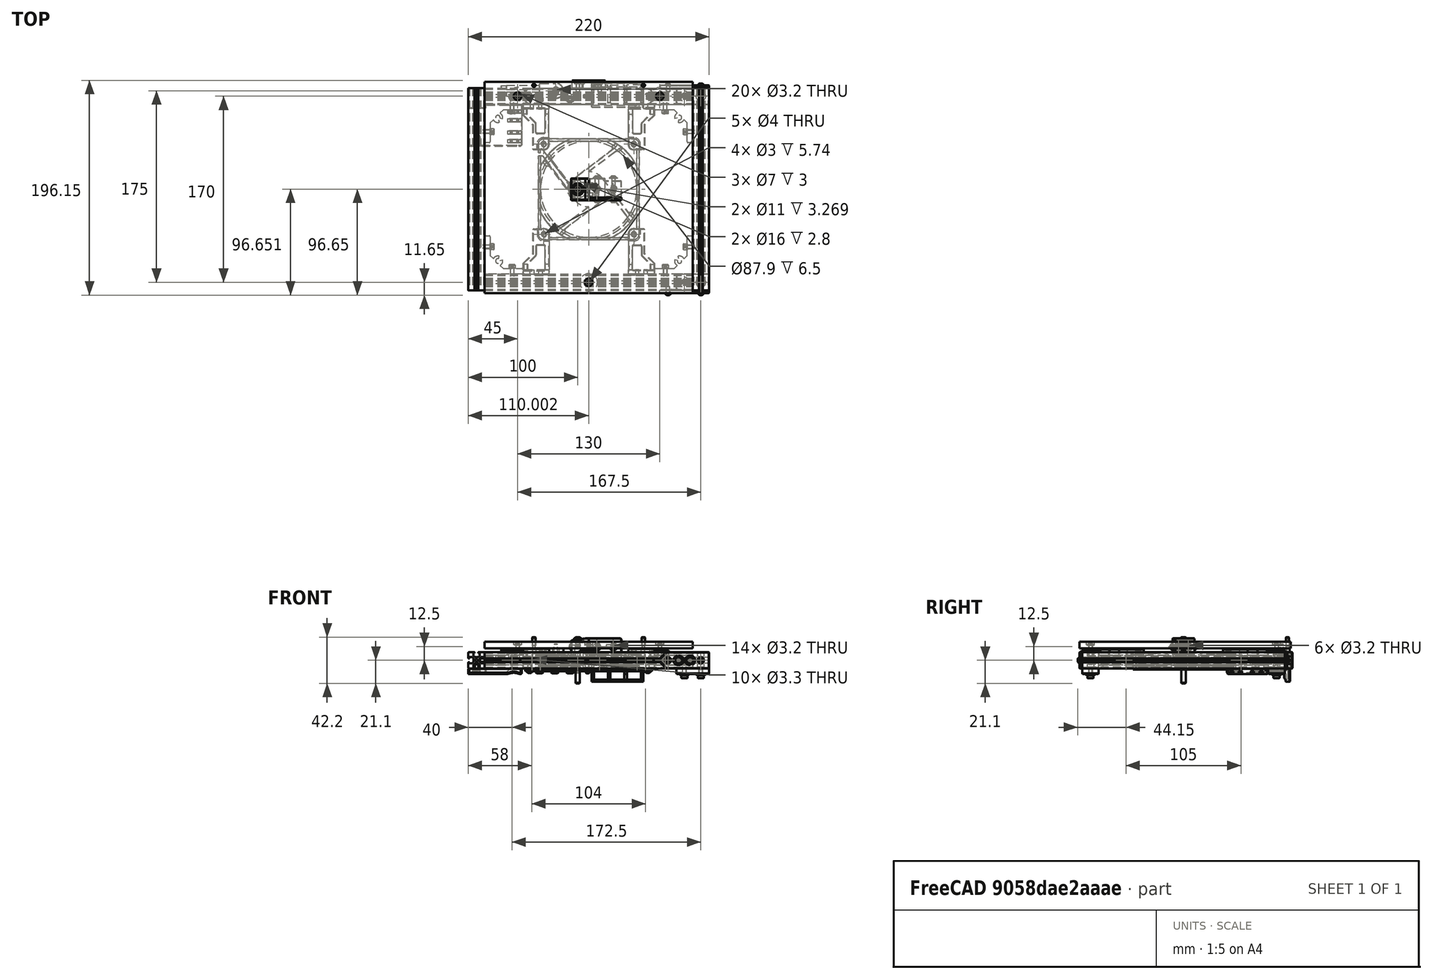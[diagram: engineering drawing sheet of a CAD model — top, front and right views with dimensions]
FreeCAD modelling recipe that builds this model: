
FCSTD DOCUMENT  (FreeCAD 0.19R24291 (Git))
Label: bed-assembly
License: Other
LicenseURL: GPL3
objects: Part::FeaturePython×88, Part::Feature×34, App::Part×8, PartDesign::CoordinateSystem×1
note: 123 computed .brp shape members not serialized (recipe doc carries the construction recipe); baked Part::Feature solids carry a one-line shape summary decoded from their .brp

FEATURE [Part::Feature] Cut028006004005011004003001010002002002001001  label="frame-end-cap"
  Placement = pos=(110,-95,-7.5) rot=(0,0.707107,0.707107;3.14159rad)
  shape: bbox 45 x 3.5 x 15 mm, 345 faces (baked)
FEATURE [Part::Feature] Chamfer004013007011015006009007001005003046001001  label="extrusion-connector"
  Placement = pos=(110,-77.5,-12.5) rot=(0,0,1;3.14159rad)
  shape: bbox 30 x 15 x 6 mm, 55 faces (baked)
FEATURE [Part::Feature] Extrude001001  label="1515-185mm001"
  Placement = pos=(102.5,92.5,-2.1e-14) rot=(1,0,0;1.5708rad)
  shape: bbox 15 x 185 x 15 mm, 71 faces (baked)
FEATURE [Part::Feature] Extrude001002  label="1515-190mm001"
  Placement = pos=(-95,-85,-2.11e-14) rot=(0,1,0;1.5708rad)
  shape: bbox 190 x 15 x 15 mm, 71 faces (baked)
FEATURE [Part::Feature] Extrude001005  label="1515-185mm003"
  Placement = pos=(-102.5,92.5,-2.1e-14) rot=(1,0,0;1.5708rad)
  shape: bbox 15 x 185 x 15 mm, 71 faces (baked)
FEATURE [Part::Feature] Extrude001006  label="1515-190mm003"
  Placement = pos=(-95,85,-2.11e-14) rot=(0,1,0;1.5708rad)
  shape: bbox 190 x 15 x 15 mm, 71 faces (baked)
FEATURE [Part::Feature] Part__Feature006  label="HBLTBS008"
  Placement = pos=(95,77.5,2.1e-14) rot=(0.707107,0,-0.707107;3.14159rad)
  shape: bbox 35 x 35 x 9 mm, 26 faces (baked)
FEATURE [Part::Feature] Part__Feature005  label="HBLTBS007"
  Placement = pos=(-95,77.5,-2.1e-14) rot=(0.57735,0.57735,-0.57735;2.0944rad)
  shape: bbox 35 x 35 x 9 mm, 26 faces (baked)
FEATURE [Part::Feature] Part__Feature008  label="HBLTBS010"
  Placement = pos=(-95,-77.5,-2.11e-14) rot=(0,1,0;1.5708rad)
  shape: bbox 35 x 35 x 9 mm, 26 faces (baked)
FEATURE [Part::Feature] Part__Feature007  label="HBLTBS009"
  Placement = pos=(95,-77.5,2.1e-14) rot=(0.57735,-0.57735,-0.57735;4.18879rad)
  shape: bbox 35 x 35 x 9 mm, 26 faces (baked)
FEATURE [Part::FeaturePython] Washer012  label="M3-Washer018"  # Fasteners workbench fastener (typed FeaturePython)
  Placement = pos=(-90,52.5,-2.1e-14) rot=(0,1,0;1.5708rad)
  baseObject = -> Part__Feature005 [Edge27]
  diameter = 4
  invert = false
  leftHanded = false
  matchOuter = true
  offset = 0
  type = 5
FEATURE [Part::FeaturePython] Washer013  label="M3-Washer019"  # Fasteners workbench fastener (typed FeaturePython)
  Placement = pos=(-70,72.5,-2.1e-14) rot=(1,0,0;1.5708rad)
  baseObject = -> Part__Feature005 [Edge62]
  diameter = 4
  invert = true
  leftHanded = false
  matchOuter = true
  offset = 0
  type = 5
FEATURE [Part::FeaturePython] Washer014  label="M3-Washer022"  # Fasteners workbench fastener (typed FeaturePython)
  Placement = pos=(90,52.5,2e-14) rot=(0,-1,0;1.5708rad)
  baseObject = -> Part__Feature006 [Edge62]
  diameter = 4
  invert = true
  leftHanded = false
  matchOuter = true
  offset = 0
  type = 5
FEATURE [Part::FeaturePython] Washer015  label="M3-Washer021"  # Fasteners workbench fastener (typed FeaturePython)
  Placement = pos=(70,72.5,1.5e-14) rot=(1,0,0;1.5708rad)
  baseObject = -> Part__Feature006 [Edge27]
  diameter = 4
  invert = false
  leftHanded = false
  matchOuter = true
  offset = 0
  type = 5
FEATURE [Part::FeaturePython] Washer016  label="M3-Washer023"  # Fasteners workbench fastener (typed FeaturePython)
  Placement = pos=(90,-52.5,2.1e-14) rot=(0,-1,0;1.5708rad)
  baseObject = -> Part__Feature007 [Edge27]
  diameter = 4
  invert = false
  leftHanded = false
  matchOuter = true
  offset = 0
  type = 5
FEATURE [Part::FeaturePython] Washer017  label="M3-Washer024"  # Fasteners workbench fastener (typed FeaturePython)
  Placement = pos=(70,-72.5,2.1e-14) rot=(-1,0,0;1.5708rad)
  baseObject = -> Part__Feature007 [Edge62]
  diameter = 4
  invert = true
  leftHanded = false
  matchOuter = true
  offset = 0
  type = 5
FEATURE [Part::FeaturePython] Washer018  label="M3-Washer025"  # Fasteners workbench fastener (typed FeaturePython)
  Placement = pos=(-70,-72.5,-2.1e-14) rot=(-1,0,0;1.5708rad)
  baseObject = -> Part__Feature008 [Edge27]
  diameter = 4
  invert = false
  leftHanded = false
  matchOuter = true
  offset = 0
  type = 5
FEATURE [Part::FeaturePython] Washer019  label="M3-Washer026"  # Fasteners workbench fastener (typed FeaturePython)
  Placement = pos=(-90,-52.5,-2.1e-14) rot=(0,1,0;1.5708rad)
  baseObject = -> Part__Feature008 [Edge62]
  diameter = 4
  invert = true
  leftHanded = false
  matchOuter = true
  offset = 0
  type = 5
FEATURE [Part::FeaturePython] Screw025  label="M3x10-Screw008"  # Fasteners workbench fastener (typed FeaturePython)
  Placement = pos=(-70,-71.95,-2.09e-14) rot=(-1,0,0;1.5708rad)
  baseObject = -> Washer018 [Edge1]
  diameter = 4
  invert = false
  leftHanded = false
  length = 3
  lengthCustom = 10
  matchOuter = true
  offset = 0
  thread = false
  type = 34
FEATURE [Part::FeaturePython] Screw026  label="M3x10-Screw009"  # Fasteners workbench fastener (typed FeaturePython)
  Placement = pos=(-89.45,-52.5,-2.09e-14) rot=(0,1,0;1.5708rad)
  baseObject = -> Washer019 [Edge1]
  diameter = 4
  invert = false
  leftHanded = false
  length = 3
  lengthCustom = 10
  matchOuter = true
  offset = 0
  thread = false
  type = 34
FEATURE [Part::FeaturePython] Screw027  label="M3x10-Screw010"  # Fasteners workbench fastener (typed FeaturePython)
  Placement = pos=(-89.45,52.5,-2.09e-14) rot=(0,1,0;1.5708rad)
  baseObject = -> Washer012 [Edge1]
  diameter = 4
  invert = false
  leftHanded = false
  length = 3
  lengthCustom = 10
  matchOuter = true
  offset = 0
  thread = false
  type = 34
FEATURE [Part::FeaturePython] Screw028  label="M3x10-Screw011"  # Fasteners workbench fastener (typed FeaturePython)
  Placement = pos=(-70,71.95,-2.09e-14) rot=(1,0,0;1.5708rad)
  baseObject = -> Washer013 [Edge1]
  diameter = 4
  invert = false
  leftHanded = false
  length = 3
  lengthCustom = 10
  matchOuter = true
  offset = 0
  thread = false
  type = 34
FEATURE [Part::FeaturePython] Screw029  label="M3x10-Screw012"  # Fasteners workbench fastener (typed FeaturePython)
  Placement = pos=(70,71.95,1.6e-14) rot=(1,0,0;1.5708rad)
  baseObject = -> Washer015 [Edge1]
  diameter = 4
  invert = false
  leftHanded = false
  length = 3
  lengthCustom = 10
  matchOuter = true
  offset = 0
  thread = false
  type = 34
FEATURE [Part::FeaturePython] Screw030  label="M3x10-Screw013"  # Fasteners workbench fastener (typed FeaturePython)
  Placement = pos=(89.45,52.5,2e-14) rot=(0,-1,0;1.5708rad)
  baseObject = -> Washer014 [Edge1]
  diameter = 4
  invert = false
  leftHanded = false
  length = 3
  lengthCustom = 10
  matchOuter = true
  offset = 0
  thread = false
  type = 34
FEATURE [Part::FeaturePython] Screw031  label="M3x10-Screw014"  # Fasteners workbench fastener (typed FeaturePython)
  Placement = pos=(89.45,-52.5,2.11e-14) rot=(0,-1,0;1.5708rad)
  baseObject = -> Washer016 [Edge1]
  diameter = 4
  invert = false
  leftHanded = false
  length = 3
  lengthCustom = 10
  matchOuter = true
  offset = 0
  thread = false
  type = 34
FEATURE [Part::FeaturePython] Screw032  label="M3x10-Screw015"  # Fasteners workbench fastener (typed FeaturePython)
  Placement = pos=(70,-71.95,2.11e-14) rot=(-1,0,0;1.5708rad)
  baseObject = -> Washer017 [Edge1]
  diameter = 4
  invert = false
  leftHanded = false
  length = 3
  lengthCustom = 10
  matchOuter = true
  offset = 0
  thread = false
  type = 34
FEATURE [Part::Feature] Chamfer004013007011015006009007001005003063003001002001002001005001006  label="extrusion-connector001"
  Placement = pos=(110,92.5,-12.5) rot=(0,0,1;3.14159rad)
  shape: bbox 30 x 15 x 6 mm, 55 faces (baked)
FEATURE [Part::FeaturePython] Washer020  label="M3-Washer027"  # Fasteners workbench fastener (typed FeaturePython)
  Placement = pos=(87.5,-85,-12.5) rot=(1,0,0;3.14159rad)
  baseObject = -> Chamfer004013007011015006009007001005003046001001 [Edge61]
  diameter = 1
  invert = true
  leftHanded = false
  matchOuter = true
  offset = 0
  type = 6
FEATURE [Part::FeaturePython] Washer021  label="M3-Washer028"  # Fasteners workbench fastener (typed FeaturePython)
  Placement = pos=(102.5,-85,-12.5) rot=(1,0,0;3.14159rad)
  baseObject = -> Chamfer004013007011015006009007001005003046001001 [Edge62]
  diameter = 1
  invert = true
  leftHanded = false
  matchOuter = true
  offset = 0
  type = 6
FEATURE [Part::FeaturePython] Washer022  label="M3-Washer029"  # Fasteners workbench fastener (typed FeaturePython)
  Placement = pos=(87.5,85,-12.5) rot=(1,0,0;3.14159rad)
  baseObject = -> Chamfer004013007011015006009007001005003063003001002001002001005001006 [Edge61]
  diameter = 1
  invert = true
  leftHanded = false
  matchOuter = true
  offset = 0
  type = 6
FEATURE [Part::FeaturePython] Washer023  label="M3-Washer030"  # Fasteners workbench fastener (typed FeaturePython)
  Placement = pos=(102.5,85,-12.5) rot=(1,0,0;3.14159rad)
  baseObject = -> Chamfer004013007011015006009007001005003063003001002001002001005001006 [Edge62]
  diameter = 1
  invert = true
  leftHanded = false
  matchOuter = true
  offset = 0
  type = 6
FEATURE [Part::FeaturePython] Screw033  label="M3x10-Screw016"  # Fasteners workbench fastener (typed FeaturePython)
  Placement = pos=(87.5,-85,-13.4) rot=(1,0,0;3.14159rad)
  baseObject = -> Washer020 [Edge1]
  diameter = 4
  invert = false
  leftHanded = false
  length = 3
  lengthCustom = 10
  matchOuter = true
  offset = 0
  thread = false
  type = 34
FEATURE [Part::FeaturePython] Screw034  label="M3x10-Screw017"  # Fasteners workbench fastener (typed FeaturePython)
  Placement = pos=(102.5,-85,-13.4) rot=(1,0,0;3.14159rad)
  baseObject = -> Washer021 [Edge1]
  diameter = 4
  invert = false
  leftHanded = false
  length = 3
  lengthCustom = 10
  matchOuter = true
  offset = 0
  thread = false
  type = 34
FEATURE [Part::FeaturePython] Screw035  label="M3x10-Screw018"  # Fasteners workbench fastener (typed FeaturePython)
  Placement = pos=(87.5,85,-13.4) rot=(1,0,0;3.14159rad)
  baseObject = -> Washer022 [Edge1]
  diameter = 4
  invert = false
  leftHanded = false
  length = 3
  lengthCustom = 10
  matchOuter = true
  offset = 0
  thread = false
  type = 34
FEATURE [Part::FeaturePython] Screw036  label="M3x10-Screw019"  # Fasteners workbench fastener (typed FeaturePython)
  Placement = pos=(102.5,85,-13.4) rot=(1,0,0;3.14159rad)
  baseObject = -> Washer023 [Edge1]
  diameter = 4
  invert = false
  leftHanded = false
  length = 3
  lengthCustom = 10
  matchOuter = true
  offset = 0
  thread = false
  type = 34
FEATURE [Part::Feature] Cut028006004005011004003001010002002002001007  label="frame-end-cap001"
  Placement = pos=(110,95,7.5) rot=(0,0.707107,-0.707107;3.14159rad)
  shape: bbox 45 x 3.5 x 15 mm, 345 faces (baked)
FEATURE [Part::FeaturePython] Screw037  label="M3x6-Screw006"  # Fasteners workbench fastener (typed FeaturePython)
  Placement = pos=(102.5,95,-1.07e-13) rot=(-1,0,0;1.5708rad)
  baseObject = -> Cut028006004005011004003001010002002002001007 [Edge235]
  diameter = 1
  invert = true
  leftHanded = false
  length = 0
  lengthCustom = 6
  matchOuter = true
  offset = 0
  thread = false
  type = 40
FEATURE [Part::FeaturePython] Screw038  label="M3x6-Screw007"  # Fasteners workbench fastener (typed FeaturePython)
  Placement = pos=(72.5,95,-1.04e-13) rot=(-1,0,0;1.5708rad)
  baseObject = -> Cut028006004005011004003001010002002002001007 [Edge236]
  diameter = 1
  invert = true
  leftHanded = false
  length = 0
  lengthCustom = 6
  matchOuter = true
  offset = 0
  thread = false
  type = 40
FEATURE [Part::FeaturePython] Screw039  label="M3x6-Screw008"  # Fasteners workbench fastener (typed FeaturePython)
  Placement = pos=(72.5,-95,-6.8e-14) rot=(1,0,0;1.5708rad)
  baseObject = -> Cut028006004005011004003001010002002002001001 [Edge236]
  diameter = 1
  invert = true
  leftHanded = false
  length = 0
  lengthCustom = 6
  matchOuter = true
  offset = 0
  thread = false
  type = 40
FEATURE [Part::FeaturePython] Screw040  label="M3x6-Screw009"  # Fasteners workbench fastener (typed FeaturePython)
  Placement = pos=(102.5,-95,-6.5e-14) rot=(1,0,0;1.5708rad)
  baseObject = -> Cut028006004005011004003001010002002002001001 [Edge235]
  diameter = 1
  invert = true
  leftHanded = false
  length = 0
  lengthCustom = 6
  matchOuter = true
  offset = 0
  thread = false
  type = 40
FEATURE [App::Part] Part003  label="bed-frame"
  Group = -> [Extrude001001,Extrude001002,Extrude001005,Extrude001006,Part__Feature006,Part__Feature005,Part__Feature008,Part__Feature007,Chamfer004013007011015006009007001005003046001001,Chamfer004013007011015006009007001005003063003001002001002001005001006,Washer012,Washer013,Washer014,Washer015,Washer016,Washer017,Washer018,Washer019,Screw025,Screw026,Screw027,Screw028,Screw029,Screw030,Screw031,Screw032,+14 more]
  Origin = -> Origin003
FEATURE [Part::Feature] Pocket002  label="aluminum-plate-190x193x6"
  Placement = pos=(0,0,11) rot=(0,0,1;0rad)
  shape: bbox 190 x 193 x 6 mm, 17 faces (baked)
FEATURE [Part::Feature] Cut002  label="silicon-spacer001"
  Placement = pos=(-65,85,0) rot=(0,0,1;0rad)
  shape: bbox 16 x 16 x 9 mm, 4 faces (baked)
FEATURE [Part::Feature] Cut003  label="silicon-spacer002"
  Placement = pos=(0,-85,0) rot=(0,0,1;0rad)
  shape: bbox 16 x 16 x 9 mm, 4 faces (baked)
FEATURE [Part::Feature] Cut001  label="silicon-spacer"
  Placement = pos=(65,85,0) rot=(0,0,1;0rad)
  shape: bbox 16 x 16 x 9 mm, 4 faces (baked)
FEATURE [Part::FeaturePython] Washer024  label="M3-Washer031"  # Fasteners workbench fastener (typed FeaturePython)
  Placement = pos=(-65,85,9) rot=(0,0,1;0rad)
  baseObject = -> Cut002 [Edge4]
  diameter = 1
  invert = false
  leftHanded = false
  matchOuter = true
  offset = 0
  type = 6
FEATURE [Part::FeaturePython] Washer025  label="M3-Washer032"  # Fasteners workbench fastener (typed FeaturePython)
  Placement = pos=(65,85,9) rot=(0,0,1;0rad)
  baseObject = -> Cut001 [Edge4]
  diameter = 1
  invert = false
  leftHanded = false
  matchOuter = true
  offset = 0
  type = 6
FEATURE [Part::FeaturePython] Washer026  label="M3-Washer033"  # Fasteners workbench fastener (typed FeaturePython)
  Placement = pos=(0,-85,9) rot=(0,0,1;0rad)
  baseObject = -> Cut003 [Edge4]
  diameter = 1
  invert = false
  leftHanded = false
  matchOuter = true
  offset = 0
  type = 6
FEATURE [Part::FeaturePython] Washer027  label="M3-Washer034"  # Fasteners workbench fastener (typed FeaturePython)
  Placement = pos=(-65,85,9.9) rot=(0,0,1;0rad)
  baseObject = -> Washer024 [Edge1]
  diameter = 1
  invert = false
  leftHanded = false
  matchOuter = true
  offset = 0
  type = 6
FEATURE [Part::FeaturePython] Washer028  label="M3-Washer035"  # Fasteners workbench fastener (typed FeaturePython)
  Placement = pos=(0,-85,9.9) rot=(0,0,1;0rad)
  baseObject = -> Washer026 [Edge1]
  diameter = 1
  invert = false
  leftHanded = false
  matchOuter = true
  offset = 0
  type = 6
FEATURE [Part::FeaturePython] Washer029  label="M3-Washer036"  # Fasteners workbench fastener (typed FeaturePython)
  Placement = pos=(65,85,9.9) rot=(0,0,1;0rad)
  baseObject = -> Washer025 [Edge1]
  diameter = 1
  invert = false
  leftHanded = false
  matchOuter = true
  offset = 0
  type = 6
FEATURE [Part::FeaturePython] Screw041  label="M3x16-Screw"  # Fasteners workbench fastener (typed FeaturePython)
  Placement = pos=(-65,85,13.8) rot=(0,0,1;0rad)
  baseObject = -> Washer027 [Edge1]
  diameter = 1
  invert = false
  leftHanded = false
  length = 5
  lengthCustom = 16
  matchOuter = true
  offset = 3
  thread = false
  type = 40
FEATURE [Part::FeaturePython] Screw042  label="M3x16-Screw003"  # Fasteners workbench fastener (typed FeaturePython)
  Placement = pos=(65,85,13.8) rot=(0,0,1;0rad)
  baseObject = -> Washer029 [Edge1]
  diameter = 1
  invert = false
  leftHanded = false
  length = 5
  lengthCustom = 16
  matchOuter = true
  offset = 3
  thread = false
  type = 40
FEATURE [Part::FeaturePython] Screw043  label="M3x16-Screw004"  # Fasteners workbench fastener (typed FeaturePython)
  Placement = pos=(0,-85,13.8) rot=(0,0,1;0rad)
  baseObject = -> Washer028 [Edge1]
  diameter = 1
  invert = false
  leftHanded = false
  length = 5
  lengthCustom = 16
  matchOuter = true
  offset = 3
  thread = false
  type = 40
FEATURE [Part::FeaturePython] Screw044  label="M3x8-Screw002"  # Fasteners workbench fastener (typed FeaturePython)
  Placement = pos=(-50,95,21) rot=(0,0,1;0rad)
  baseObject = -> Pocket002 [Edge21]
  diameter = 6
  invert = false
  leftHanded = false
  length = 5
  lengthCustom = 8
  matchOuter = true
  offset = 4
  thread = false
  type = 30
FEATURE [Part::FeaturePython] Screw045  label="M3x8-Screw003"  # Fasteners workbench fastener (typed FeaturePython)
  Placement = pos=(50,95,21) rot=(0,0,1;0rad)
  baseObject = -> Pocket002 [Edge20]
  diameter = 6
  invert = false
  leftHanded = false
  length = 5
  lengthCustom = 8
  matchOuter = true
  offset = 4
  thread = false
  type = 30
FEATURE [Part::Feature] Part__Feature004  label="thermal-fuse-180"
  Placement = pos=(-30,90,11.18) rot=(0,1,0;1.5708rad)
  shape: bbox 57 x 14 x 6 mm, 31 faces (baked)
FEATURE [Part::FeaturePython] Washer030  label="M3-Washer037"  # Fasteners workbench fastener (typed FeaturePython)
  Placement = pos=(-30,90,5.18) rot=(1,0,0;3.14159rad)
  baseObject = -> Part__Feature004 [Edge27]
  diameter = 4
  invert = false
  leftHanded = false
  matchOuter = true
  offset = 0
  type = 5
FEATURE [Part::FeaturePython] Screw046  label="M3x10-Screw020"  # Fasteners workbench fastener (typed FeaturePython)
  Placement = pos=(-30,90,4.63) rot=(1,0,0;3.14159rad)
  baseObject = -> Washer030 [Edge1]
  diameter = 4
  invert = false
  leftHanded = false
  length = 3
  lengthCustom = 10
  matchOuter = true
  offset = 0
  thread = false
  type = 34
FEATURE [App::Part] Part004  label="bed-plate"
  Group = -> [Pocket002,Cut002,Cut003,Cut001,Washer024,Washer025,Washer026,Washer027,Washer028,Washer029,Screw041,Screw042,Screw043,Screw044,Screw045,Part__Feature004,Washer030,Screw046]
  Origin = -> Origin004
  Placement = pos=(0,0,7.5) rot=(0,0,1;0rad)
FEATURE [Part::Feature] Part__Mirroring002  label="wago-mounter"
  Placement = pos=(0,75,-7.5) rot=(1,0,0;3.14159rad)
  shape: bbox 116 x 22.25 x 12.2 mm, 276 faces (baked)
FEATURE [Part::Feature] Body001001001  label="bed-cable-supporter"
  Placement = pos=(0,92.5,-7.5) rot=(0,0,1;0rad)
  shape: bbox 30 x 8 x 15 mm, 58 faces (baked)
FEATURE [Part::FeaturePython] Screw047  label="M3x6-Screw013"  # Fasteners workbench fastener (typed FeaturePython)
  Placement = pos=(-54,85,-10) rot=(1,0,0;3.14159rad)
  baseObject = -> Part__Mirroring002 [Edge150]
  diameter = 1
  invert = true
  leftHanded = false
  length = 0
  lengthCustom = 6
  matchOuter = true
  offset = 0
  thread = false
  type = 40
FEATURE [Part::FeaturePython] Screw048  label="M3x6-Screw014"  # Fasteners workbench fastener (typed FeaturePython)
  Placement = pos=(-10,85,-10) rot=(1,0,0;3.14159rad)
  baseObject = -> Part__Mirroring002 [Edge178]
  diameter = 1
  invert = true
  leftHanded = false
  length = 0
  lengthCustom = 6
  matchOuter = true
  offset = 0
  thread = false
  type = 40
FEATURE [Part::FeaturePython] Screw049  label="M3x6-Screw015"  # Fasteners workbench fastener (typed FeaturePython)
  Placement = pos=(54,85,-10) rot=(1,0,0;3.14159rad)
  baseObject = -> Part__Mirroring002 [Edge651]
  diameter = 1
  invert = true
  leftHanded = false
  length = 0
  lengthCustom = 6
  matchOuter = true
  offset = 0
  thread = false
  type = 40
FEATURE [Part::FeaturePython] Screw052  label="M3x8-Screw001"  # Fasteners workbench fastener (typed FeaturePython)
  Placement = pos=(-10,96.5,-1e-15) rot=(-1,0,0;1.5708rad)
  baseObject = -> Body001001001 [Edge118]
  diameter = 4
  invert = true
  leftHanded = false
  length = 2
  lengthCustom = 8
  matchOuter = true
  offset = 0
  thread = false
  type = 34
FEATURE [Part::FeaturePython] Screw053  label="M3x8-Screw"  # Fasteners workbench fastener (typed FeaturePython)
  Placement = pos=(10,96.5,-1e-15) rot=(-1,0,0;1.5708rad)
  baseObject = -> Body001001001 [Edge80]
  diameter = 4
  invert = true
  leftHanded = false
  length = 2
  lengthCustom = 8
  matchOuter = true
  offset = 0
  thread = false
  type = 34
FEATURE [Part::Feature] Body002001003  label="1515-92mm-fan-mount002"
  Placement = pos=(-59.75,-77.5,10.5) rot=(1,0,0;3.14159rad)
  shape: bbox 23.75 x 42.25 x 18 mm, 72 faces (baked)
FEATURE [Part::Feature] Part__Mirroring001003  label="1515-92mm-fan-mount001 (Mirror #1)002"
  Placement = pos=(-60,77.5,10.5) rot=(1,0,0;3.14159rad)
  shape: bbox 23.75 x 42.25 x 18 mm, 72 faces (baked)
FEATURE [Part::Feature] Body002001  label="1515-92mm-fan-mount001"
  Placement = pos=(60,77.5,10.5) rot=(0,1,0;3.14159rad)
  shape: bbox 23.75 x 42.25 x 18 mm, 72 faces (baked)
FEATURE [Part::Feature] Part__Mirroring003  label="1515-92mm-fan-mount001 (Mirror #1)001"
  Placement = pos=(60,-77.5,10.5) rot=(0,1,0;3.14159rad)
  shape: bbox 23.75 x 42.25 x 18 mm, 72 faces (baked)
FEATURE [Part::Feature] Fusion001001  label="92mm-slim-fan"
  Placement = pos=(0,2e-15,7.5) rot=(1,0,0;3.14159rad)
  shape: bbox 118.8 x 118.8 x 17.52 mm, 159 faces (baked)
FEATURE [Part::FeaturePython] HeatSet009  label="M3x4-HeatSet006"  # WARN: FeaturePython — macro-defined, semantics opaque (R4)
  Placement = pos=(41.25,-41.25,5.5) rot=(1,0,0;3.14159rad)
  baseObject = -> Part__Mirroring003 [Edge125]
  diameter = 2
  invert = true
  leftHanded = false
  offset = 0
FEATURE [Part::FeaturePython] HeatSet010  label="M3x4-HeatSet007"  # WARN: FeaturePython — macro-defined, semantics opaque (R4)
  Placement = pos=(-41,-41.25,5.5) rot=(1,0,0;3.14159rad)
  baseObject = -> Body002001003 [Edge125]
  diameter = 2
  invert = false
  leftHanded = false
  offset = 0
FEATURE [Part::FeaturePython] HeatSet011  label="M3x4-HeatSet008"  # WARN: FeaturePython — macro-defined, semantics opaque (R4)
  Placement = pos=(-41.25,41.25,5.5) rot=(1,0,0;3.14159rad)
  baseObject = -> Part__Mirroring001003 [Edge125]
  diameter = 2
  invert = true
  leftHanded = false
  offset = 0
FEATURE [Part::FeaturePython] HeatSet012  label="M3x4-HeatSet009"  # WARN: FeaturePython — macro-defined, semantics opaque (R4)
  Placement = pos=(41.25,41.25,5.5) rot=(1,0,0;3.14159rad)
  baseObject = -> Body002001 [Edge125]
  diameter = 2
  invert = false
  leftHanded = false
  offset = 0
FEATURE [App::Part] Part006  label="bed-fan"
  Group = -> [Body002001003,Part__Mirroring001003,Body002001,Part__Mirroring003,Fusion001001,HeatSet009,HeatSet010,HeatSet011,HeatSet012]
  Origin = -> Origin006
FEATURE [PartDesign::CoordinateSystem] LCS_0  label="LCS_bed"
  AttacherType = Attacher::AttachEngine3D
  MapMode = 2
  Support = -> [X_Axis007]
FEATURE [Part::FeaturePython] Screw054  label="M3x6-Screw018"  # Fasteners workbench fastener (typed FeaturePython)
  Placement = pos=(-102.5,67.5,-9.5) rot=(1,0,0;3.14159rad)
  diameter = 1
  invert = false
  leftHanded = false
  length = 0
  lengthCustom = 6
  matchOuter = true
  offset = 0
  thread = false
  type = 40
FEATURE [Part::FeaturePython] Screw055  label="M3x6-Screw019"  # Fasteners workbench fastener (typed FeaturePython)
  Placement = pos=(-102.5,46.5,-9.5) rot=(1,0,0;3.14159rad)
  diameter = 1
  invert = false
  leftHanded = false
  length = 0
  lengthCustom = 6
  matchOuter = true
  offset = 0
  thread = false
  type = 40
FEATURE [Part::Feature] Fusion001001001  label="bed-cable-mounter"
  Placement = pos=(-110,77.5,-12.5) rot=(1,0,0;1.5708rad)
  shape: bbox 49 x 38 x 5 mm, 109 faces (baked)
FEATURE [App::Part] Part005  label="bed-cable-management"
  Group = -> [Part__Mirroring002,Body001001001,Screw047,Screw048,Screw049,Screw053,Screw052,Screw054,Screw055,Fusion001001001]
  Origin = -> Origin005
FEATURE [Part::Feature] Chamfer004013007011015006009007001005003063003001002001002001007002017001  label="front-left-arm"
  shape: bbox 49.5 x 20 x 20 mm, 120 faces (baked)
FEATURE [Part::Feature] Part__Mirroring001001  label="back-left-arm"
  Placement = pos=(0,0,0) rot=(0,0,1;3.14159rad)
  shape: bbox 49.5 x 20 x 20 mm, 120 faces (baked)
FEATURE [Part::Feature] Body004001  label="middle-right-arm"
  shape: bbox 34.5 x 20 x 20 mm, 89 faces (baked)
FEATURE [Part::Feature] Tube001001  label="silicon-spacer-16ODx4UDx9H001"
  Placement = pos=(-10,0,-4) rot=(0,0,1;0rad)
  shape: bbox 16 x 16 x 7 mm, 4 faces (baked)
FEATURE [Part::Feature] Tube001002  label="silicon-spacer-16ODx4UDx9H002"
  Placement = pos=(-10,0,-4) rot=(0,0,1;0rad)
  shape: bbox 16 x 16 x 7 mm, 4 faces (baked)
FEATURE [Part::Feature] Tube001003  label="silicon-spacer-16ODx4UDx9H003"
  Placement = pos=(-10,0,-4) rot=(0,0,1;0rad)
  shape: bbox 16 x 16 x 7 mm, 4 faces (baked)
FEATURE [Part::Feature] Tube001002001  label="O-ring-10ODx4IDx2H001"
  Placement = pos=(-10,0,16) rot=(0,0,1;0rad)
  shape: bbox 10 x 10 x 2 mm, 4 faces (baked)
FEATURE [Part::Feature] Tube001002002  label="O-ring-10ODx4IDx2H002"
  Placement = pos=(-10,0,16) rot=(0,0,1;0rad)
  shape: bbox 10 x 10 x 2 mm, 4 faces (baked)
FEATURE [Part::Feature] Tube001002003  label="O-ring-10ODx4IDx2H003"
  Placement = pos=(-10,0,16) rot=(0,0,1;0rad)
  shape: bbox 10 x 10 x 2 mm, 4 faces (baked)
FEATURE [Part::FeaturePython] Washer  label="M3-Washer"  # Fasteners workbench fastener (typed FeaturePython)
  Placement = pos=(7.5,0,0) rot=(-1,0,0;3.14159rad)
  baseObject = -> Chamfer004013007011015006009007001005003063003001002001002001007002017001 [Edge223]
  diameter = 4
  invert = false
  leftHanded = false
  matchOuter = false
  offset = 0
  type = 3
FEATURE [Part::FeaturePython] Washer031  label="M3-Washer038"  # Fasteners workbench fastener (typed FeaturePython)
  Placement = pos=(22.5,0,0) rot=(-1,0,0;3.14159rad)
  baseObject = -> Chamfer004013007011015006009007001005003063003001002001002001007002017001 [Edge222]
  diameter = 4
  invert = false
  leftHanded = false
  matchOuter = false
  offset = 0
  type = 3
FEATURE [Part::FeaturePython] Washer032  label="M3-Washer042"  # Fasteners workbench fastener (typed FeaturePython)
  Placement = pos=(7.5,-9e-16,0) rot=(-1,0,0;3.14159rad)
  baseObject = -> Part__Mirroring001001 [Edge223]
  diameter = 4
  invert = true
  leftHanded = false
  matchOuter = false
  offset = 0
  type = 3
FEATURE [Part::FeaturePython] Washer033  label="M3-Washer043"  # Fasteners workbench fastener (typed FeaturePython)
  Placement = pos=(22.5,-2.8e-15,0) rot=(-1,0,0;3.14159rad)
  baseObject = -> Part__Mirroring001001 [Edge222]
  diameter = 4
  invert = true
  leftHanded = false
  matchOuter = false
  offset = 0
  type = 3
FEATURE [Part::FeaturePython] Washer034  label="M3-Washer041"  # Fasteners workbench fastener (typed FeaturePython)
  Placement = pos=(7.5,0,0) rot=(-1,0,0;3.14159rad)
  baseObject = -> Body004001 [Edge68]
  diameter = 4
  invert = false
  leftHanded = false
  matchOuter = false
  offset = 0
  type = 3
FEATURE [Part::FeaturePython] Screw  label="M3x10-Screw"  # Fasteners workbench fastener (typed FeaturePython)
  Placement = pos=(7.5,1e-16,-0.55) rot=(-1,0,0;3.14159rad)
  baseObject = -> Washer [Edge1]
  diameter = 3
  invert = false
  leftHanded = false
  length = 3
  lengthCustom = 10
  matchOuter = false
  offset = 0
  thread = false
  type = 22
FEATURE [Part::FeaturePython] Screw056  label="M3x10-Screw021"  # Fasteners workbench fastener (typed FeaturePython)
  Placement = pos=(22.5,1e-16,-0.55) rot=(-1,0,0;3.14159rad)
  baseObject = -> Washer031 [Edge1]
  diameter = 3
  invert = false
  leftHanded = false
  length = 3
  lengthCustom = 10
  matchOuter = false
  offset = 0
  thread = false
  type = 22
FEATURE [Part::FeaturePython] Screw057  label="M3x10-Screw022"  # Fasteners workbench fastener (typed FeaturePython)
  Placement = pos=(7.5,-9e-16,-0.55) rot=(-1,0,0;3.14159rad)
  baseObject = -> Washer032 [Edge1]
  diameter = 4
  invert = false
  leftHanded = false
  length = 3
  lengthCustom = 10
  matchOuter = false
  offset = 0
  thread = false
  type = 36
FEATURE [Part::FeaturePython] Screw058  label="M3x10-Screw023"  # Fasteners workbench fastener (typed FeaturePython)
  Placement = pos=(22.5,-2.7e-15,-0.55) rot=(-1,0,0;3.14159rad)
  baseObject = -> Washer033 [Edge1]
  diameter = 4
  invert = false
  leftHanded = false
  length = 3
  lengthCustom = 10
  matchOuter = false
  offset = 0
  thread = false
  type = 36
FEATURE [Part::FeaturePython] Screw059  label="M3x10-Screw024"  # Fasteners workbench fastener (typed FeaturePython)
  Placement = pos=(7.5,1e-16,-0.55) rot=(-1,0,0;3.14159rad)
  baseObject = -> Washer034 [Edge1]
  diameter = 4
  invert = false
  leftHanded = false
  length = 3
  lengthCustom = 10
  matchOuter = false
  offset = 0
  thread = false
  type = 36
FEATURE [Part::FeaturePython] Washer035  label="M3-Washer044"  # Fasteners workbench fastener (typed FeaturePython)
  Placement = pos=(7.5,-10,12.5) rot=(1,0,0;1.5708rad)
  baseObject = -> Chamfer004013007011015006009007001005003063003001002001002001007002017001 [Edge59]
  diameter = 4
  invert = false
  leftHanded = false
  matchOuter = true
  offset = 0
  type = 3
FEATURE [Part::FeaturePython] Washer036  label="M3-Washer045"  # Fasteners workbench fastener (typed FeaturePython)
  Placement = pos=(22.5,-10,12.5) rot=(1,0,0;1.5708rad)
  baseObject = -> Chamfer004013007011015006009007001005003063003001002001002001007002017001 [Edge60]
  diameter = 4
  invert = false
  leftHanded = false
  matchOuter = true
  offset = 0
  type = 3
FEATURE [Part::FeaturePython] Washer037  label="M3-Washer048"  # Fasteners workbench fastener (typed FeaturePython)
  Placement = pos=(22.5,10,12.5) rot=(-1,0,0;1.5708rad)
  baseObject = -> Part__Mirroring001001 [Edge60]
  diameter = 4
  invert = true
  leftHanded = false
  matchOuter = true
  offset = 0
  type = 3
FEATURE [Part::FeaturePython] Washer038  label="M3-Washer049"  # Fasteners workbench fastener (typed FeaturePython)
  Placement = pos=(7.5,10,12.5) rot=(-1,0,0;1.5708rad)
  baseObject = -> Part__Mirroring001001 [Edge59]
  diameter = 4
  invert = true
  leftHanded = false
  matchOuter = true
  offset = 0
  type = 3
FEATURE [Part::FeaturePython] Screw060  label="M3x8-Screw004"  # Fasteners workbench fastener (typed FeaturePython)
  Placement = pos=(7.5,-10.55,12.5) rot=(1,0,0;1.5708rad)
  baseObject = -> Washer035 [Edge1]
  diameter = 1
  invert = false
  leftHanded = false
  length = 1
  lengthCustom = 8
  matchOuter = true
  offset = 0
  thread = false
  type = 42
FEATURE [Part::FeaturePython] Screw061  label="M3x8-Screw005"  # Fasteners workbench fastener (typed FeaturePython)
  Placement = pos=(22.5,-10.55,12.5) rot=(1,0,0;1.5708rad)
  baseObject = -> Washer036 [Edge1]
  diameter = 1
  invert = false
  leftHanded = false
  length = 1
  lengthCustom = 8
  matchOuter = true
  offset = 0
  thread = false
  type = 42
FEATURE [Part::FeaturePython] Screw062  label="M3x8-Screw006"  # Fasteners workbench fastener (typed FeaturePython)
  Placement = pos=(22.5,10.55,12.5) rot=(-1,0,0;1.5708rad)
  baseObject = -> Washer037 [Edge1]
  diameter = 1
  invert = false
  leftHanded = false
  length = 1
  lengthCustom = 8
  matchOuter = true
  offset = 0
  thread = false
  type = 42
FEATURE [Part::FeaturePython] Screw063  label="M3x8-Screw007"  # Fasteners workbench fastener (typed FeaturePython)
  Placement = pos=(7.5,10.55,12.5) rot=(-1,0,0;1.5708rad)
  baseObject = -> Washer038 [Edge1]
  diameter = 1
  invert = false
  leftHanded = false
  length = 1
  lengthCustom = 8
  matchOuter = true
  offset = 0
  thread = false
  type = 42
FEATURE [Part::FeaturePython] Washer039  label="M4-OD10-Washer-001"  # Fasteners workbench fastener (typed FeaturePython)
  Placement = pos=(-10,0,18) rot=(0,0,1;0rad)
  baseObject = -> Tube001002001 [Edge4]
  diameter = 5
  invert = false
  leftHanded = false
  matchOuter = true
  offset = 0
  type = 3
FEATURE [Part::FeaturePython] Washer040  label="M4-OD10-Washer"  # Fasteners workbench fastener (typed FeaturePython)
  Placement = pos=(-10,0,18) rot=(0,0,1;0rad)
  baseObject = -> Tube001002002 [Edge4]
  diameter = 5
  invert = false
  leftHanded = false
  matchOuter = true
  offset = 0
  type = 3
FEATURE [Part::FeaturePython] Washer041  label="M4-OD10-Washer001"  # Fasteners workbench fastener (typed FeaturePython)
  Placement = pos=(-10,0,18) rot=(0,0,1;0rad)
  baseObject = -> Tube001002003 [Edge4]
  diameter = 5
  invert = false
  leftHanded = false
  matchOuter = true
  offset = 0
  type = 3
FEATURE [Part::FeaturePython] Screw064  label="M4x40-Screw"  # Fasteners workbench fastener (typed FeaturePython)
  Placement = pos=(-10,0,18.9) rot=(0,0,1;0rad)
  baseObject = -> Washer039 [Edge1]
  diameter = 2
  invert = false
  leftHanded = false
  length = 10
  lengthCustom = 40
  matchOuter = true
  offset = 0
  thread = false
  type = 42
FEATURE [Part::FeaturePython] Screw065  label="M4x40-Screw001"  # Fasteners workbench fastener (typed FeaturePython)
  Placement = pos=(-10,0,18.9) rot=(0,0,1;0rad)
  baseObject = -> Washer040 [Edge1]
  diameter = 2
  invert = false
  leftHanded = false
  length = 10
  lengthCustom = 40
  matchOuter = true
  offset = 0
  thread = false
  type = 42
FEATURE [Part::FeaturePython] Screw066  label="M4x40-Screw002"  # Fasteners workbench fastener (typed FeaturePython)
  Placement = pos=(-10,0,18.9) rot=(0,0,1;0rad)
  baseObject = -> Washer041 [Edge1]
  diameter = 2
  invert = false
  leftHanded = false
  length = 10
  lengthCustom = 40
  matchOuter = true
  offset = 0
  thread = false
  type = 42
FEATURE [Part::FeaturePython] Washer042  label="M3-Washer052"  # Fasteners workbench fastener (typed FeaturePython)
  Placement = pos=(-15.5,-4.5,12.5) rot=(0,-1,0;1.5708rad)
  baseObject = -> Chamfer004013007011015006009007001005003063003001002001002001007002017001 [Edge126]
  diameter = 4
  invert = true
  leftHanded = false
  matchOuter = true
  offset = 0
  type = 3
FEATURE [Part::FeaturePython] Washer043  label="M3-Washer053"  # Fasteners workbench fastener (typed FeaturePython)
  Placement = pos=(-15.5,4.5,12.5) rot=(0,-1,0;1.5708rad)
  baseObject = -> Chamfer004013007011015006009007001005003063003001002001002001007002017001 [Edge138]
  diameter = 4
  invert = true
  leftHanded = false
  matchOuter = true
  offset = 0
  type = 3
FEATURE [Part::FeaturePython] Washer044  label="M3-Washer054"  # Fasteners workbench fastener (typed FeaturePython)
  Placement = pos=(-15.5,4.5,12.5) rot=(0,-1,0;1.5708rad)
  baseObject = -> Part__Mirroring001001 [Edge126]
  diameter = 4
  invert = false
  leftHanded = false
  matchOuter = true
  offset = 0
  type = 3
FEATURE [Part::FeaturePython] Washer045  label="M3-Washer055"  # Fasteners workbench fastener (typed FeaturePython)
  Placement = pos=(-15.5,-4.5,12.5) rot=(0,-1,0;1.5708rad)
  baseObject = -> Part__Mirroring001001 [Edge138]
  diameter = 4
  invert = false
  leftHanded = false
  matchOuter = true
  offset = 0
  type = 3
FEATURE [Part::FeaturePython] Washer046  label="M3-Washer058"  # Fasteners workbench fastener (typed FeaturePython)
  Placement = pos=(-15.5,4.5,12.5) rot=(0,-1,0;1.5708rad)
  baseObject = -> Body004001 [Edge129]
  diameter = 4
  invert = true
  leftHanded = false
  matchOuter = true
  offset = 0
  type = 3
FEATURE [Part::FeaturePython] Washer047  label="M3-Washer057"  # Fasteners workbench fastener (typed FeaturePython)
  Placement = pos=(-15.5,-4.5,12.5) rot=(0,-1,0;1.5708rad)
  baseObject = -> Body004001 [Edge127]
  diameter = 4
  invert = true
  leftHanded = false
  matchOuter = true
  offset = 0
  type = 3
FEATURE [Part::FeaturePython] Screw067  label="M3x20-Screw"  # Fasteners workbench fastener (typed FeaturePython)
  Placement = pos=(-16.05,-4.5,12.5) rot=(0,-1,0;1.5708rad)
  baseObject = -> Washer042 [Edge1]
  diameter = 1
  invert = false
  leftHanded = false
  length = 6
  lengthCustom = 20
  matchOuter = true
  offset = 0
  thread = false
  type = 42
FEATURE [Part::FeaturePython] Screw068  label="M3x20-Screw001"  # Fasteners workbench fastener (typed FeaturePython)
  Placement = pos=(-16.05,4.5,12.5) rot=(0,-1,0;1.5708rad)
  baseObject = -> Washer043 [Edge1]
  diameter = 1
  invert = false
  leftHanded = false
  length = 6
  lengthCustom = 20
  matchOuter = true
  offset = 0
  thread = false
  type = 42
FEATURE [App::Part] Part  label="bed-arm-front-left"
  Group = -> [Chamfer004013007011015006009007001005003063003001002001002001007002017001,Tube001002001,Tube001001,Washer,Washer031,Screw056,Screw,Washer035,Washer036,Screw060,Screw061,Washer039,Screw064,Washer042,Washer043,Screw067,Screw068]
  Origin = -> Origin
  Placement = pos=(-110,-85,-12.5) rot=(0,0,1;0rad)
FEATURE [Part::FeaturePython] Screw069  label="M3x20-Screw002"  # Fasteners workbench fastener (typed FeaturePython)
  Placement = pos=(-16.05,-4.5,12.5) rot=(0,-1,0;1.5708rad)
  baseObject = -> Washer045 [Edge1]
  diameter = 1
  invert = false
  leftHanded = false
  length = 6
  lengthCustom = 20
  matchOuter = true
  offset = 0
  thread = false
  type = 42
FEATURE [Part::FeaturePython] Screw070  label="M3x20-Screw003"  # Fasteners workbench fastener (typed FeaturePython)
  Placement = pos=(-16.05,4.5,12.5) rot=(0,-1,0;1.5708rad)
  baseObject = -> Washer044 [Edge1]
  diameter = 1
  invert = false
  leftHanded = false
  length = 6
  lengthCustom = 20
  matchOuter = true
  offset = 0
  thread = false
  type = 42
FEATURE [App::Part] Part001  label="bed-arm-back-left"
  Group = -> [Part__Mirroring001001,Tube001002,Tube001002002,Washer032,Washer033,Screw058,Screw057,Washer037,Washer038,Screw063,Screw062,Washer040,Screw065,Washer045,Washer044,Screw070,Screw069]
  Origin = -> Origin001
  Placement = pos=(-110,85,-12.5) rot=(0,0,1;0rad)
FEATURE [Part::FeaturePython] Screw071  label="M3x20-Screw004"  # Fasteners workbench fastener (typed FeaturePython)
  Placement = pos=(-16.05,4.5,12.5) rot=(0,-1,0;1.5708rad)
  baseObject = -> Washer046 [Edge1]
  diameter = 1
  invert = false
  leftHanded = false
  length = 6
  lengthCustom = 20
  matchOuter = true
  offset = 0
  thread = false
  type = 42
FEATURE [Part::FeaturePython] Screw072  label="M3x20-Screw005"  # Fasteners workbench fastener (typed FeaturePython)
  Placement = pos=(-16.05,-4.5,12.5) rot=(0,-1,0;1.5708rad)
  baseObject = -> Washer047 [Edge1]
  diameter = 1
  invert = false
  leftHanded = false
  length = 6
  lengthCustom = 20
  matchOuter = true
  offset = 0
  thread = false
  type = 42
FEATURE [App::Part] Part002  label="bed-arm-mid-right"
  Group = -> [Body004001,Tube001003,Tube001002003,Washer034,Screw059,Washer041,Screw066,Washer047,Washer046,Screw071,Screw072]
  Origin = -> Origin002
  Placement = pos=(110,-4.7e-15,-12.5) rot=(0,0,1;3.14159rad)
FEATURE [App::Part] bed_assembly
  Group = -> [LCS_0,Part,Part001,Part002,Part003,Part004,Part005,Part006]
  Origin = -> Origin007
